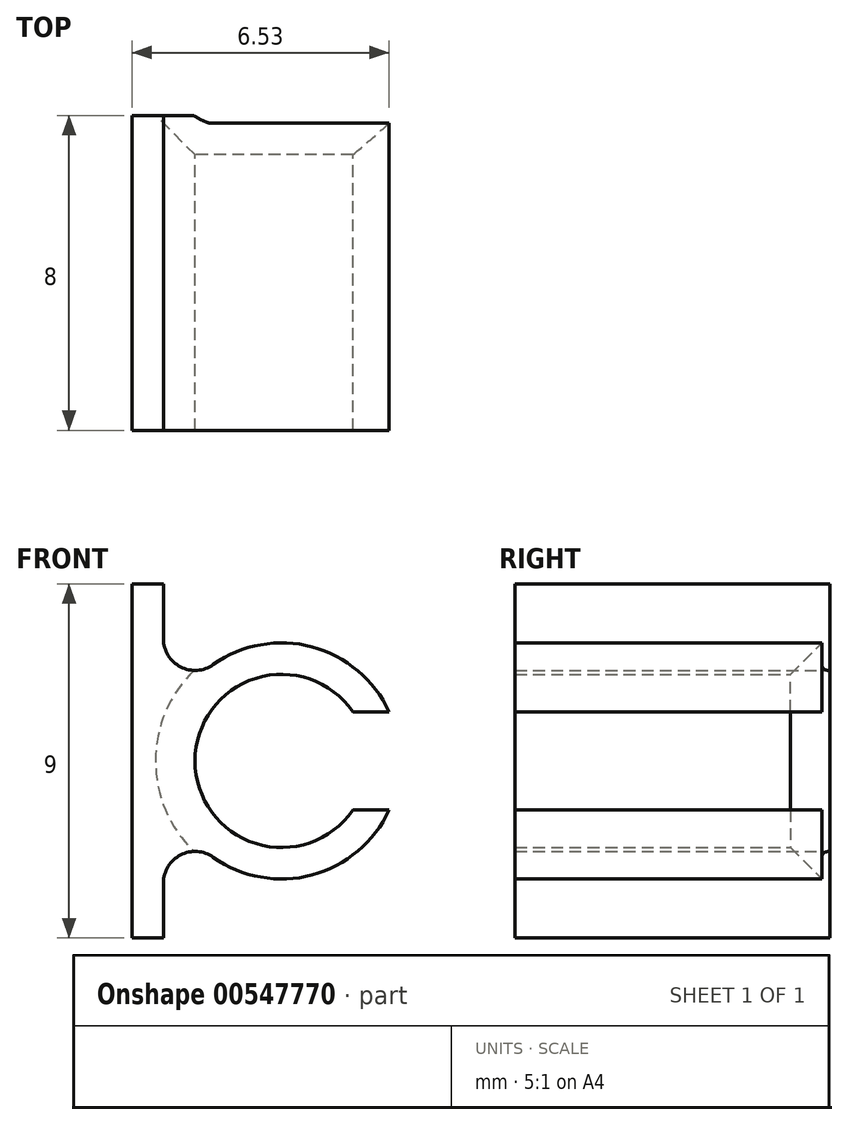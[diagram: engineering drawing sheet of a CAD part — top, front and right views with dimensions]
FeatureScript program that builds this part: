
annotation { "Feature Type Name" : "Feature", "Feature Type Description" : "" }
export const myFeature = defineFeature(function(context is Context, id is Id, definition is map)
    precondition{}
    {
        {
            var Q0;
            Q0=qCreatedBy(makeId("Front.planeOp"),FACE);
            var sketch = newSketch(context, id + "F0", { "sketchPlane" : qUnion([Q0])});
            skLineSegment(sketch, "E0", {"start": v(0, 0) * mm, "end": v(3.8, 0) * mm, "construction": true});
            skLineSegment(sketch, "E1", {"start": v(0, 0) * mm, "end": v(0, 4.5) * mm});
            skLineSegment(sketch, "E2", {"start": v(0, 4.5) * mm, "end": v(0.8, 4.5) * mm});
            skLineSegment(sketch, "E3", {"start": v(0.8, 4.5) * mm, "end": v(0.8, 3.1) * mm});
            skCircle(sketch, "E4", {"center": v(3.8, 0) * mm, "radius": 2.2 * mm});
            skArc(sketch, "E5", {"start": v(2.06, -2.45) * mm, "mid": v(6.8, 0) * mm, "end": v(2.06, 2.45) * mm});
            skArc(sketch, "E6", {"start": v(0.8, 3.1) * mm, "mid": v(1.23, 2.39) * mm, "end": v(2.06, 2.45) * mm});
            skLineSegment(sketch, "E7.bottom", {"start": v(4.42, 1.25) * mm, "end": v(9.69, 1.25) * mm});
            skLineSegment(sketch, "E7.top", {"start": v(4.42, -1.25) * mm, "end": v(9.69, -1.25) * mm});
            skLineSegment(sketch, "E7.left", {"start": v(4.42, 1.25) * mm, "end": v(4.42, -1.25) * mm});
            skLineSegment(sketch, "E7.right", {"start": v(9.69, 1.25) * mm, "end": v(9.69, -1.25) * mm});
            skPoint(sketch, "E7.middle", {"position": v(7.06, 0) * mm});
            skArc(sketch, "E8.MirrorCS", {"start": v(0.8, -3.1) * mm, "mid": v(1.23, -2.39) * mm, "end": v(2.06, -2.45) * mm});
            skLineSegment(sketch, "E9.MirrorCS", {"start": v(0.8, -4.5) * mm, "end": v(0.8, -3.1) * mm});
            skLineSegment(sketch, "E10.MirrorCS", {"start": v(0, -4.5) * mm, "end": v(0.8, -4.5) * mm});
            skLineSegment(sketch, "E11.MirrorCS", {"start": v(0, 0) * mm, "end": v(0, -4.5) * mm});
            skPoint(sketch, "E12.orphan", {"position": v(0.8, 0) * mm});
            skSolve(sketch);
        }
        {
            var Q0;
            Q0=makeQuery(id+"F0.imprint","IMPRINT",FACE,{"disambiguationData":[TD([[makeQuery(id+"F0.imprint","IMPRINT",EDGE,{"derivedFrom":sQuery(id+"F0.wireOp",EDGE,"E1")}),-1.0]])]});
            extrude(context, id + "F1", {"entities" : qUnion([Q0]), "depth" : 8 * mm, "offsetDistance" : 25 * mm});
        }
        {
            var Q0;
            Q0=makeQuery(id+"F1.opExtrude","CAP_EDGE",EDGE,{"disambiguationData":[OSD([sQuery(id+"F0.wireOp",EDGE,"E4")])],"isStart":true});
            chamfer(context, id + "F2", {"entities" : qUnion([Q0]), "width" : 1 * mm, "tangentPropagation" : true});
        }
    });
